# Revit family: LeL Colorado 3.2
name_source: partatom
category: Lighting Fixtures
units: mm (PartAtom-declared; Revit-internal decimal feet)

## family parameters
Always vertical = No
Cut with Voids When Loaded = No
Light Source = No
OmniClass Number = 23.80.70.00
OmniClass Title = Lighting
Part Type = Normal
Room Calculation Point = No
Round Connector Dimension = Use Diameter
Shared = No
Work Plane-Based = Yes

## types (6) — shared parameters
Alimentazione = 230 V
Apparent Load = 83 VA
CCT = 3000 K
CRI = CRI80
Default Elevation = 1219 mm
Description = Outdoor/projectors
Finish = LeL Black
IK = IK09
IP = IP65 IP67 IP69
Lamp = LED
Manufacturer = L&L Luce&Light srl
Model = CA32
Rated Power supply = 230 V
URL = https://www.lucelight.it
Wattage = 83 W
Weight = 10.00 kg

## per-type parameters (varying)
| type | Lumen Output | Optic |
| 3.2 W 15°x50° 83W | 6922 lm | COLORADO Light source : 3.2 W 15°x50° 83W |
| 3.2 D 83W | 4510 lm | COLORADO Light source : 3.2 D 83W |
| 3.2 K 76° 83W | 7032 lm | COLORADO Light source : 3.2 K 76° 83W |
| 3.2 L 45° 83W | 6990 lm | COLORADO Light source : 3.2 L 45° 83W |
| 3.2 M 30° 83W | 7074 lm | COLORADO Light source : 3.2 M 30° 83W |
| 3.2 S 12° 83W | 7286 lm | COLORADO Light source : 3.2 S 12° 83W |

## geometry (parser evidence)
native form markers: Sweep x3
no freeform markers — native parametric forms only
